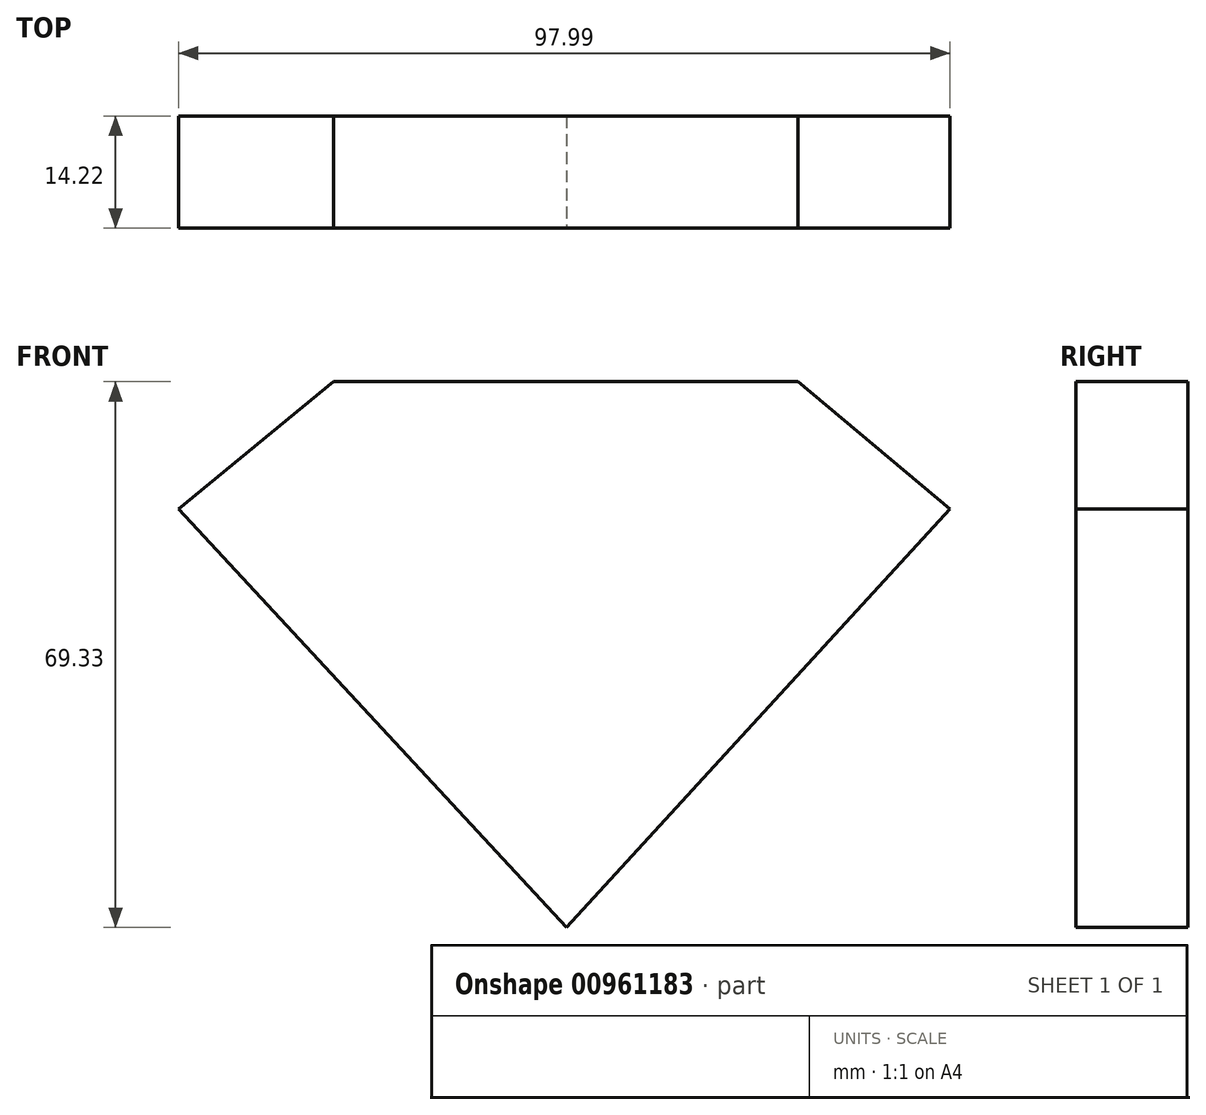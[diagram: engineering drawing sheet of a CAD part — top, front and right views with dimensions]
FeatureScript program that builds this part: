
annotation { "Feature Type Name" : "Feature", "Feature Type Description" : "" }
export const myFeature = defineFeature(function(context is Context, id is Id, definition is map)
    precondition{}
    {
        {
            var Q0;
            Q0=qCreatedBy(makeId("Front.planeOp"),FACE);
            var sketch = newSketch(context, id + "F0", { "sketchPlane" : qUnion([Q0])});
            skLineSegment(sketch, "E0", {"start": v(0, -39.72) * mm, "end": v(-49.3, 13.7) * mm});
            skLineSegment(sketch, "E1", {"start": v(-49.3, 13.7) * mm, "end": v(-29.62, 29.89) * mm});
            skLineSegment(sketch, "E2", {"start": v(-29.62, 29.89) * mm, "end": v(29.12, 29.89) * mm});
            skLineSegment(sketch, "E3", {"start": v(29.12, 29.89) * mm, "end": v(48.7, 13.76) * mm});
            skLineSegment(sketch, "E4", {"start": v(48.7, 13.76) * mm, "end": v(0, -39.72) * mm});
            skLineSegment(sketch, "E5", {"start": v(14.9, 21.95) * mm, "end": v(19.07, 18.34) * mm});
            skLineSegment(sketch, "E6", {"start": v(19.07, 18.34) * mm, "end": v(19.7, 21.91) * mm});
            skLineSegment(sketch, "E7", {"start": v(19.7, 21.91) * mm, "end": v(14.9, 21.95) * mm});
            skLineSegment(sketch, "E8", {"start": v(19.84, 16.2) * mm, "end": v(20.8, 22.94) * mm});
            skLineSegment(sketch, "E9", {"start": v(20.8, 22.94) * mm, "end": v(10.7, 22.94) * mm});
            skLineSegment(sketch, "E10", {"start": v(10.7, 22.94) * mm, "end": v(10.7, 22.72) * mm});
            skArc(sketch, "E11", {"start": v(17.64, 18.42) * mm, "mid": v(14.45, 21.02) * mm, "end": v(10.7, 22.72) * mm});
            skLineSegment(sketch, "E12", {"start": v(17.64, 18.42) * mm, "end": v(19.84, 16.2) * mm});
            skLineSegment(sketch, "E13", {"start": v(-38.3, 13.38) * mm, "end": v(-26.9, 23) * mm});
            skLineSegment(sketch, "E14", {"start": v(-26.9, 23) * mm, "end": v(-17.35, 23) * mm});
            skLineSegment(sketch, "E15", {"start": v(-17.35, 23) * mm, "end": v(-17.35, 22.83) * mm});
            skArc(sketch, "E16", {"start": v(-17.35, 22.83) * mm, "mid": v(-21.65, 21.09) * mm, "end": v(-25.56, 18.6) * mm});
            skArc(sketch, "E17", {"start": v(-25.56, 18.6) * mm, "mid": v(-28.82, 15.54) * mm, "end": v(-30.77, 11.5) * mm});
            skArc(sketch, "E18", {"start": v(-30.77, 11.5) * mm, "mid": v(-31.25, 8.58) * mm, "end": v(-31, 5.62) * mm});
            skLineSegment(sketch, "E19", {"start": v(-38.3, 13.38) * mm, "end": v(-31, 5.62) * mm});
            skArc(sketch, "E20", {"start": v(-25.94, 19.53) * mm, "mid": v(-30.4, 14.64) * mm, "end": v(-32.16, 8.26) * mm});
            skLineSegment(sketch, "E21", {"start": v(-25.94, 19.53) * mm, "end": v(-21.73, 21.95) * mm});
            skLineSegment(sketch, "E22", {"start": v(-21.73, 21.95) * mm, "end": v(-26.6, 21.95) * mm});
            skLineSegment(sketch, "E23", {"start": v(-26.6, 21.95) * mm, "end": v(-36.89, 13.27) * mm});
            skLineSegment(sketch, "E24", {"start": v(-36.89, 13.27) * mm, "end": v(-32.16, 8.26) * mm});
            skArc(sketch, "E25", {"start": v(26.96, 3.37) * mm, "mid": v(22.48, 7.33) * mm, "end": v(16.93, 9.53) * mm});
            skArc(sketch, "E26", {"start": v(16.93, 9.53) * mm, "mid": v(10.46, 10.28) * mm, "end": v(3.95, 10.5) * mm});
            skArc(sketch, "E27", {"start": v(-5.93, 10.8) * mm, "mid": v(-1, 10.54) * mm, "end": v(3.95, 10.5) * mm});
            skArc(sketch, "E28", {"start": v(-12.67, 11.7) * mm, "mid": v(-9.34, 10.97) * mm, "end": v(-5.93, 10.8) * mm});
            skArc(sketch, "E29", {"start": v(-16.5, 13.44) * mm, "mid": v(-14.67, 12.38) * mm, "end": v(-12.67, 11.7) * mm});
            skArc(sketch, "E30", {"start": v(-15.77, 18.56) * mm, "mid": v(-17.53, 16.2) * mm, "end": v(-16.5, 13.44) * mm});
            skArc(sketch, "E31", {"start": v(1.08, 21.89) * mm, "mid": v(-7.68, 21.93) * mm, "end": v(-15.77, 18.56) * mm});
            skArc(sketch, "E32", {"start": v(10.38, 18.36) * mm, "mid": v(5.98, 20.8) * mm, "end": v(1.08, 21.89) * mm});
            skArc(sketch, "E33", {"start": v(13.79, 11.93) * mm, "mid": v(12.73, 15.49) * mm, "end": v(10.38, 18.36) * mm});
            skLineSegment(sketch, "E34", {"start": v(13.79, 11.93) * mm, "end": v(28.82, 11.93) * mm});
            skLineSegment(sketch, "E35", {"start": v(28.82, 11.93) * mm, "end": v(28.82, 19.33) * mm});
            skLineSegment(sketch, "E36", {"start": v(28.82, 19.33) * mm, "end": v(35.99, 13.2) * mm});
            skLineSegment(sketch, "E37", {"start": v(35.99, 13.2) * mm, "end": v(26.96, 3.37) * mm});
            skArc(sketch, "E38", {"start": v(14.68, 12.9) * mm, "mid": v(12.56, 17.6) * mm, "end": v(8.44, 20.73) * mm});
            skArc(sketch, "E39", {"start": v(8.44, 20.73) * mm, "mid": v(3.1, 22.6) * mm, "end": v(-2.52, 23.13) * mm});
            skArc(sketch, "E40", {"start": v(-2.52, 23.13) * mm, "mid": v(-5.71, 23.1) * mm, "end": v(-8.87, 22.66) * mm});
            skArc(sketch, "E41", {"start": v(-8.87, 22.66) * mm, "mid": v(-12.56, 21.47) * mm, "end": v(-16, 19.68) * mm});
            skArc(sketch, "E42", {"start": v(-16, 19.68) * mm, "mid": v(-18.17, 17.33) * mm, "end": v(-18.17, 14.14) * mm});
            skArc(sketch, "E43", {"start": v(-18.17, 14.14) * mm, "mid": v(-15.95, 11.9) * mm, "end": v(-12.98, 10.85) * mm});
            skArc(sketch, "E44", {"start": v(-12.98, 10.85) * mm, "mid": v(-9.02, 9.96) * mm, "end": v(-4.96, 9.68) * mm});
            skLineSegment(sketch, "E45", {"start": v(-4.96, 9.68) * mm, "end": v(12, 9.14) * mm});
            skArc(sketch, "E46", {"start": v(25.26, 3.8) * mm, "mid": v(19.22, 7.92) * mm, "end": v(12, 9.14) * mm});
            skLineSegment(sketch, "E47", {"start": v(25.26, 3.8) * mm, "end": v(26.92, 2.04) * mm});
            skLineSegment(sketch, "E48", {"start": v(26.92, 2.04) * mm, "end": v(37.5, 13.2) * mm});
            skLineSegment(sketch, "E49", {"start": v(37.5, 13.2) * mm, "end": v(28, 21.35) * mm});
            skLineSegment(sketch, "E50", {"start": v(28, 21.35) * mm, "end": v(28, 12.86) * mm});
            skLineSegment(sketch, "E51", {"start": v(28, 12.86) * mm, "end": v(14.68, 12.9) * mm});
            skArc(sketch, "E52", {"start": v(16.46, -6.74) * mm, "mid": v(16.93, -5.8) * mm, "end": v(16.3, -4.96) * mm});
            skArc(sketch, "E53", {"start": v(16.3, -4.96) * mm, "mid": v(13.39, -3.56) * mm, "end": v(10.19, -3.1) * mm});
            skArc(sketch, "E54", {"start": v(11.81, -9.14) * mm, "mid": v(14.26, -8.18) * mm, "end": v(16.46, -6.74) * mm});
            skArc(sketch, "E55", {"start": v(8.64, -9.76) * mm, "mid": v(10.26, -9.65) * mm, "end": v(11.81, -9.14) * mm});
            skLineSegment(sketch, "E56", {"start": v(8.64, -9.76) * mm, "end": v(-1.05, -9.76) * mm});
            skArc(sketch, "E57", {"start": v(-1.05, -9.76) * mm, "mid": v(-5.3, -6.29) * mm, "end": v(-10.66, -5.04) * mm});
            skArc(sketch, "E58", {"start": v(-10.66, -4.96) * mm, "mid": v(-14.75, -5.62) * mm, "end": v(-18.64, -7.05) * mm});
            skLineSegment(sketch, "E59", {"start": v(-18.64, -7.05) * mm, "end": v(-24.37, -0.54) * mm});
            skArc(sketch, "E60", {"start": v(-24.37, -0.54) * mm, "mid": v(-15.93, -1.9) * mm, "end": v(-7.4, -2.56) * mm});
            skArc(sketch, "E61", {"start": v(-7.4, -2.56) * mm, "mid": v(-1.4, -2.8) * mm, "end": v(4.6, -2.68) * mm});
            skArc(sketch, "E62", {"start": v(10.19, -3.1) * mm, "mid": v(7.4, -2.82) * mm, "end": v(4.6, -2.68) * mm});
            skArc(sketch, "E63", {"start": v(-1.75, -10.7) * mm, "mid": v(-5.47, -7.12) * mm, "end": v(-10.5, -5.97) * mm});
            skArc(sketch, "E64", {"start": v(-10.5, -5.97) * mm, "mid": v(-14.5, -6.53) * mm, "end": v(-18.25, -8.06) * mm});
            skArc(sketch, "E65", {"start": v(-18.61, -8.21) * mm, "mid": v(-18.43, -8.14) * mm, "end": v(-18.25, -8.06) * mm});
            skLineSegment(sketch, "E66", {"start": v(-18.61, -8.21) * mm, "end": v(-27.57, 1.58) * mm});
            skArc(sketch, "E67", {"start": v(-27.57, 1.58) * mm, "mid": v(-22.52, 0.22) * mm, "end": v(-17.37, -0.67) * mm});
            skArc(sketch, "E68", {"start": v(-17.37, -0.67) * mm, "mid": v(-13.6, -1.17) * mm, "end": v(-9.82, -1.32) * mm});
            skArc(sketch, "E69", {"start": v(8.3, -1.9) * mm, "mid": v(-0.76, -1.6) * mm, "end": v(-9.82, -1.32) * mm});
            skArc(sketch, "E70", {"start": v(12.04, -2.23) * mm, "mid": v(10.18, -1.97) * mm, "end": v(8.3, -1.9) * mm});
            skArc(sketch, "E71", {"start": v(16.18, -3.53) * mm, "mid": v(14.17, -2.7) * mm, "end": v(12.04, -2.23) * mm});
            skArc(sketch, "E72", {"start": v(18.07, -5.81) * mm, "mid": v(17.34, -4.5) * mm, "end": v(16.18, -3.53) * mm});
            skArc(sketch, "E73", {"start": v(15.82, -8.55) * mm, "mid": v(17.32, -7.49) * mm, "end": v(18.07, -5.81) * mm});
            skArc(sketch, "E74", {"start": v(8.5, -10.67) * mm, "mid": v(12.27, -9.99) * mm, "end": v(15.82, -8.55) * mm});
            skLineSegment(sketch, "E75", {"start": v(-1.75, -10.7) * mm, "end": v(8.5, -10.67) * mm});
            skArc(sketch, "E76", {"start": v(-11.64, -15.03) * mm, "mid": v(-0.2, -15.86) * mm, "end": v(11.23, -14.97) * mm});
            skLineSegment(sketch, "E77", {"start": v(11.23, -14.97) * mm, "end": v(0, -27.3) * mm});
            skLineSegment(sketch, "E78", {"start": v(0, -27.3) * mm, "end": v(-11.64, -15.03) * mm});
            skArc(sketch, "E79", {"start": v(-9.06, -16.4) * mm, "mid": v(-0.26, -16.88) * mm, "end": v(8.53, -16.4) * mm});
            skLineSegment(sketch, "E80", {"start": v(-9.06, -16.4) * mm, "end": v(-0.28, -25.67) * mm});
            skLineSegment(sketch, "E81", {"start": v(-0.28, -25.67) * mm, "end": v(8.53, -16.4) * mm});
            skSolve(sketch);
        }
        {
            var Q0;
            Q0=sQuery(id+"F0.wireOp",EDGE,"E74");
            var Q1;
            Q1=sQuery(id+"F0.wireOp",EDGE,"E71");
            var Q2;
            Q2=sQuery(id+"F0.wireOp",EDGE,"E49");
            var Q3;
            Q3=sQuery(id+"F0.wireOp",EDGE,"E29");
            var Q4;
            Q4=sQuery(id+"F0.wireOp",EDGE,"E40");
            var Q5;
            Q5=sQuery(id+"F0.wireOp",EDGE,"E69");
            var Q6;
            Q6=sQuery(id+"F0.wireOp",EDGE,"E41");
            var Q7;
            Q7=sQuery(id+"F0.wireOp",EDGE,"E44");
            var Q8;
            Q8=sQuery(id+"F0.wireOp",EDGE,"E66");
            var Q9;
            Q9=sQuery(id+"F0.wireOp",EDGE,"E13");
            var Q10;
            Q10=sQuery(id+"F0.wireOp",EDGE,"E63");
            var Q11;
            Q11=sQuery(id+"F0.wireOp",EDGE,"E25");
            var Q12;
            Q12=sQuery(id+"F0.wireOp",EDGE,"E58");
            var Q13;
            Q13=sQuery(id+"F0.wireOp",EDGE,"E60");
            var Q14;
            Q14=sQuery(id+"F0.wireOp",EDGE,"E1");
            var Q15;
            Q15=sQuery(id+"F0.wireOp",EDGE,"E68");
            var Q16;
            Q16=sQuery(id+"F0.wireOp",EDGE,"E0");
            var Q17;
            Q17=sQuery(id+"F0.wireOp",EDGE,"E57");
            var Q18;
            Q18=sQuery(id+"F0.wireOp",EDGE,"E4");
            var Q19;
            Q19=sQuery(id+"F0.wireOp",EDGE,"E22");
            var Q20;
            Q20=sQuery(id+"F0.wireOp",EDGE,"E78");
            var Q21;
            Q21=sQuery(id+"F0.wireOp",EDGE,"E27");
            var Q22;
            Q22=sQuery(id+"F0.wireOp",EDGE,"E56");
            var Q23;
            Q23=sQuery(id+"F0.wireOp",EDGE,"E42");
            var Q24;
            Q24=sQuery(id+"F0.wireOp",EDGE,"E62");
            var Q25;
            Q25=sQuery(id+"F0.wireOp",EDGE,"E17");
            var Q26;
            Q26=sQuery(id+"F0.wireOp",EDGE,"E34");
            var Q27;
            Q27=sQuery(id+"F0.wireOp",EDGE,"E16");
            var Q28;
            Q28=sQuery(id+"F0.wireOp",EDGE,"E75");
            var Q29;
            Q29=sQuery(id+"F0.wireOp",EDGE,"E24");
            var Q30;
            Q30=sQuery(id+"F0.wireOp",EDGE,"E33");
            var Q31;
            Q31=sQuery(id+"F0.wireOp",EDGE,"E51");
            var Q32;
            Q32=sQuery(id+"F0.wireOp",EDGE,"E5");
            var Q33;
            Q33=sQuery(id+"F0.wireOp",EDGE,"E79");
            var Q34;
            Q34=sQuery(id+"F0.wireOp",EDGE,"E61");
            var Q35;
            Q35=sQuery(id+"F0.wireOp",EDGE,"E77");
            var Q36;
            Q36=sQuery(id+"F0.wireOp",EDGE,"E23");
            var Q37;
            Q37=sQuery(id+"F0.wireOp",EDGE,"E6");
            var Q38;
            Q38=sQuery(id+"F0.wireOp",EDGE,"E9");
            var Q39;
            Q39=sQuery(id+"F0.wireOp",EDGE,"E80");
            var Q40;
            Q40=sQuery(id+"F0.wireOp",EDGE,"E46");
            var Q41;
            Q41=sQuery(id+"F0.wireOp",EDGE,"E3");
            var Q42;
            Q42=sQuery(id+"F0.wireOp",EDGE,"E31");
            var Q43;
            Q43=sQuery(id+"F0.wireOp",EDGE,"E19");
            var Q44;
            Q44=sQuery(id+"F0.wireOp",EDGE,"E26");
            var Q45;
            Q45=sQuery(id+"F0.wireOp",EDGE,"E7");
            var Q46;
            Q46=sQuery(id+"F0.wireOp",EDGE,"E30");
            var Q47;
            Q47=sQuery(id+"F0.wireOp",EDGE,"E20");
            var Q48;
            Q48=sQuery(id+"F0.wireOp",EDGE,"E11");
            var Q49;
            Q49=sQuery(id+"F0.wireOp",EDGE,"E36");
            var Q50;
            Q50=sQuery(id+"F0.wireOp",EDGE,"E37");
            var Q51;
            Q51=sQuery(id+"F0.wireOp",EDGE,"E35");
            var Q52;
            Q52=sQuery(id+"F0.wireOp",EDGE,"E76");
            var Q53;
            Q53=sQuery(id+"F0.wireOp",EDGE,"E64");
            var Q54;
            Q54=sQuery(id+"F0.wireOp",EDGE,"E8");
            var Q55;
            Q55=sQuery(id+"F0.wireOp",EDGE,"E45");
            var Q56;
            Q56=sQuery(id+"F0.wireOp",EDGE,"E48");
            var Q57;
            Q57=sQuery(id+"F0.wireOp",EDGE,"E14");
            var Q58;
            Q58=sQuery(id+"F0.wireOp",EDGE,"E43");
            var Q59;
            Q59=sQuery(id+"F0.wireOp",EDGE,"E50");
            var Q60;
            Q60=sQuery(id+"F0.wireOp",EDGE,"E39");
            var Q61;
            Q61=sQuery(id+"F0.wireOp",EDGE,"E53");
            var Q62;
            Q62=sQuery(id+"F0.wireOp",EDGE,"E32");
            var Q63;
            Q63=sQuery(id+"F0.wireOp",EDGE,"E21");
            var Q64;
            Q64=sQuery(id+"F0.wireOp",EDGE,"E38");
            var Q65;
            Q65=sQuery(id+"F0.wireOp",EDGE,"E2");
            var Q66;
            Q66=sQuery(id+"F0.wireOp",EDGE,"E28");
            var Q67;
            Q67=sQuery(id+"F0.wireOp",EDGE,"E81");
            var Q68;
            Q68=sQuery(id+"F0.wireOp",EDGE,"E59");
            var Q69;
            Q69=sQuery(id+"F0.wireOp",EDGE,"E67");
            var Q70;
            Q70=sQuery(id+"F0.wireOp",EDGE,"E54");
            var Q71;
            Q71=sQuery(id+"F0.wireOp",EDGE,"E55");
            var Q72;
            Q72=sQuery(id+"F0.wireOp",EDGE,"E70");
            var Q73;
            Q73=sQuery(id+"F0.wireOp",EDGE,"E73");
            var Q74;
            Q74=sQuery(id+"F0.wireOp",EDGE,"E72");
            var Q75;
            Q75=sQuery(id+"F0.wireOp",EDGE,"E12");
            var Q76;
            Q76=sQuery(id+"F0.wireOp",EDGE,"E47");
            var Q77;
            Q77=sQuery(id+"F0.wireOp",EDGE,"E10");
            var Q78;
            Q78=sQuery(id+"F0.wireOp",EDGE,"E18");
            var Q79;
            Q79=sQuery(id+"F0.wireOp",EDGE,"E52");
            var Q80;
            Q80=sQuery(id+"F0.wireOp",EDGE,"E65");
            var Q81;
            Q81=sQuery(id+"F0.wireOp",EDGE,"E15");
            extrude(context, id + "F1", {"bodyType" : ToolBodyType.SURFACE, "surfaceEntities" : qUnion([Q0, Q1, Q2, Q3, Q4, Q5, Q6, Q7, Q8, Q9, Q10, Q11, Q12, Q13, Q14, Q15, Q16, Q17, Q18, Q19, Q20, Q21, Q22, Q23, Q24, Q25, Q26, Q27, Q28, Q29, Q30, Q31, Q32, Q33, Q34, Q35, Q36, Q37, Q38, Q39, Q40, Q41, Q42, Q43, Q44, Q45, Q46, Q47, Q48, Q49, Q50, Q51, Q52, Q53, Q54, Q55, Q56, Q57, Q58, Q59, Q60, Q61, Q62, Q63, Q64, Q65, Q66, Q67, Q68, Q69, Q70, Q71, Q72, Q73, Q74, Q75, Q76, Q77, Q78, Q79, Q80, Q81]), "endBound" : BoundingType.SYMMETRIC, "depth" : 25.4 * mm, "offsetDistance" : 25.4 * mm});
        }
        {
            var Q0;
            Q0=qCreatedBy(makeId("Front.planeOp"),FACE);
            var sketch = newSketch(context, id + "F2", { "sketchPlane" : qUnion([Q0])});
            skLineSegment(sketch, "E82", {"start": v(-29.65, 30.04) * mm, "end": v(29.38, 30.04) * mm});
            skLineSegment(sketch, "E83", {"start": v(29.38, 30.04) * mm, "end": v(48.67, 13.88) * mm});
            skLineSegment(sketch, "E84", {"start": v(48.67, 13.88) * mm, "end": v(0, -39.29) * mm});
            skLineSegment(sketch, "E85", {"start": v(0, -39.29) * mm, "end": v(-49.32, 13.88) * mm});
            skLineSegment(sketch, "E86", {"start": v(-49.32, 13.88) * mm, "end": v(-29.65, 30.04) * mm});
            skSolve(sketch);
        }
        {
            var Q0;
            Q0=qSketchRegion(id+"F2",true);
            extrude(context, id + "F3", {"entities" : qUnion([Q0]), "oppositeDirection" : true, "depth" : 14.22 * mm, "offsetDistance" : 25.4 * mm});
        }
    });
